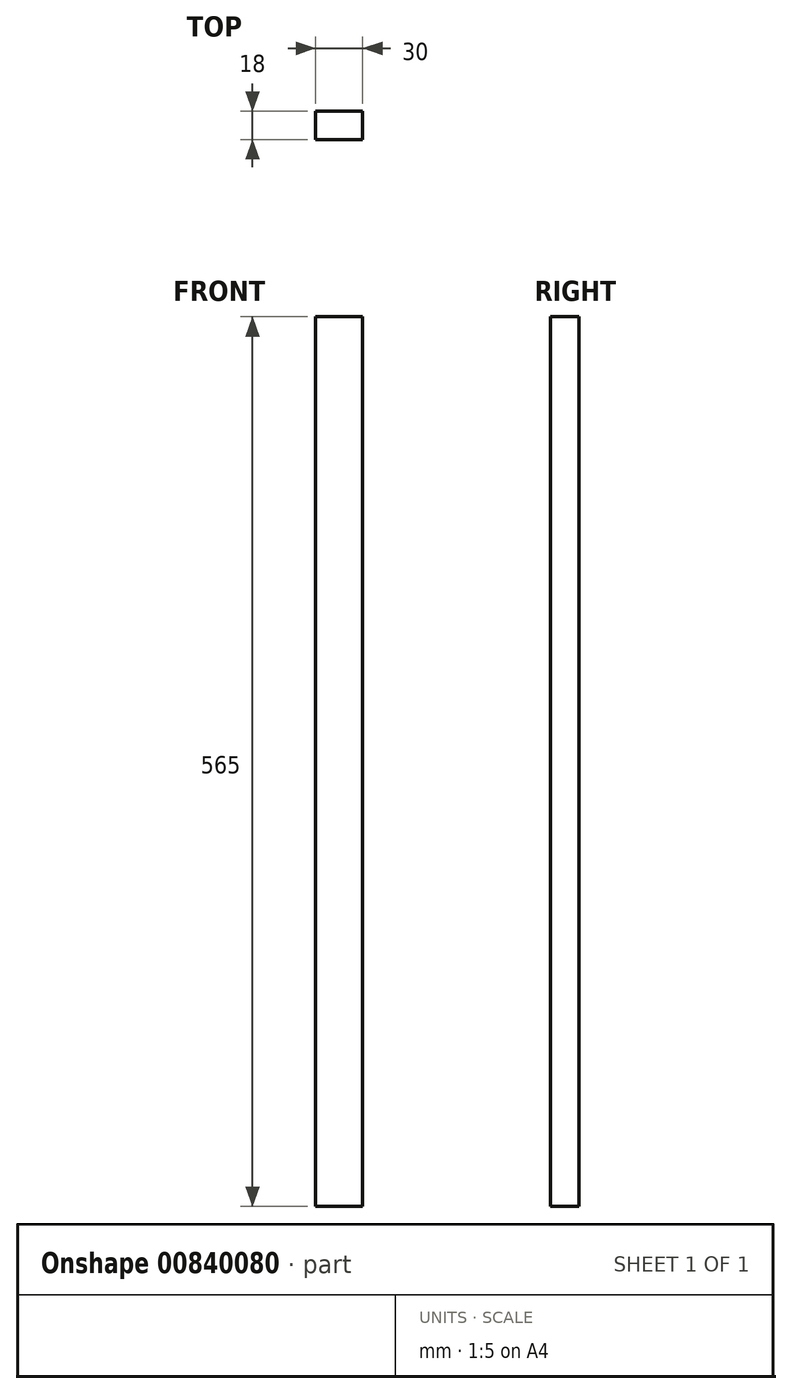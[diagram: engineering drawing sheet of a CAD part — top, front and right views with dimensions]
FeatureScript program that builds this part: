
annotation { "Feature Type Name" : "Feature", "Feature Type Description" : "" }
export const myFeature = defineFeature(function(context is Context, id is Id, definition is map)
    precondition{}
    {
        {
            var Q0;
            Q0=qCreatedBy(makeId("Front.planeOp"),FACE);
            var sketch = newSketch(context, id + "F0", { "sketchPlane" : qUnion([Q0])});
            skLineSegment(sketch, "E0.bottom", {"start": v(-15, -282.5) * mm, "end": v(15, -282.5) * mm});
            skLineSegment(sketch, "E0.top", {"start": v(-15, 282.5) * mm, "end": v(15, 282.5) * mm});
            skLineSegment(sketch, "E0.left", {"start": v(-15, -282.5) * mm, "end": v(-15, 282.5) * mm});
            skLineSegment(sketch, "E0.right", {"start": v(15, -282.5) * mm, "end": v(15, 282.5) * mm});
            skPoint(sketch, "E0.middle", {"position": v(0, 0) * mm});
            skSolve(sketch);
        }
        {
            var Q0;
            Q0=qSketchRegion(id+"F0",true);
            extrude(context, id + "F1", {"entities" : qUnion([Q0]), "oppositeDirection" : true, "depth" : 18 * mm, "offsetDistance" : 25 * mm});
        }
    });
